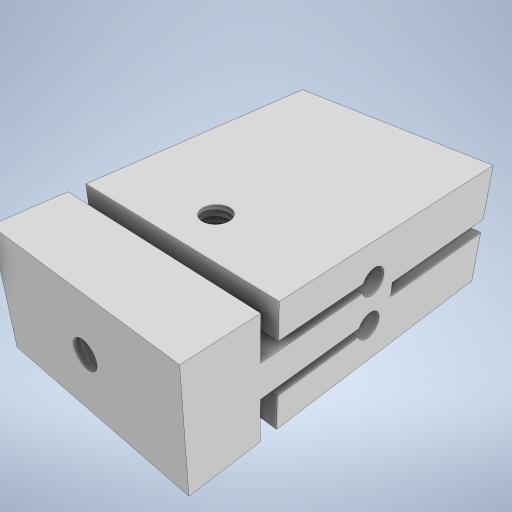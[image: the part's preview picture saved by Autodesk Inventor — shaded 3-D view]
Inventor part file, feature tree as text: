
AUTODESK INVENTOR PART (.ipt)
format: ipt  version: 2023 (Build 270158000, 158)  size: 275,968 bytes
history: native  units: mm
features: sketch x8, extrude x5, hole x3, projected_geometry x1
ambient origin geometry x8: Origin, YZ Plane, XZ Plane, XY Plane, X Axis, Y Axis, Z Axis, Center Point
bodies: Solid1 (feature_tree)
feature tree (17):
  extrude  "Extrusion1"  Depth=14.0mm
  extrude  "Extrusion2"  Depth=30.0mm
  extrude  "Extrusion3"  Depth=15.0mm TaperAngle=0.0deg
  sketch  "Sketch5"  dims[d16=5.0mm d17=3.0mm]
  hole  "Hole2"  [1 undecoded]
  hole  "Hole3"  [1 undecoded]
  extrude  "Extrusion4"  TaperAngle=0.0deg  [1 undecoded]
  extrude  "Extrusion6"  Depth=5.0mm
  hole  "Hole4"  [1 undecoded]
  sketch  "Sketch1"  dims[d0=25.0mm d1=14.0mm]
  sketch  "Sketch2"  dims[d2=30.0mm d3=0.0mm d4=30.0mm]
  sketch  "Sketch4"  dims[d5=1.6mm d6=15.0mm d7=0.0mm]
  sketch  "Sketch6"  dims[d18=3.0mm d19=1.0mm]
  sketch  "Sketch7"  dims[d20=1.0mm d21=0.0mm d22=0.0mm]
  projected_geometry  "Projected Loop1"
  sketch  "Sketch11"  dims[d23=12.0mm d24=5.0mm]
  sketch  "Sketch12"  dims[d25=3.242mm d26=8.0mm d27=4.0mm d28=2.0mm d29=90.0deg d30=8.0mm d31=0.0mm d32=3.242mm d33=8.0mm d34=4.0mm d35=2.0mm d36=90.0deg d37=8.0mm d38=0.0mm d39=2.0mm d40=0.0mm d44=8.0mm d45=0.0mm d46=3.242mm d47=6.0mm d48=4.0mm d49=2.0mm d50=90.0deg d51=7.0mm d52=0.0mm d41=0.5mm d42=0.872665mm]
note: 4 required parameter values undecoded (feature->parameter linkage not recoverable at this tier; creation-order binding heuristic only, values carry confidence <= 0.55)
